# Revit family: xTowel_Dispenser-Automatic-Bobrick-ClassicSeries-3974-150
name_source: partatom
category: Specialty Equipment
revit_build: Autodesk Revit 2014 (Build: 20130308_1515(x64)
units: mm (PartAtom-declared; Revit-internal decimal feet)

## types (1)
- 3974-150
    ADA Compliant = Yes
    Assembly Code = E20
    Default Elevation = 44"
    Description = ClassicSeries® Convertible Automatic Universal Roll Paper Towel Module
    Height = 18 1/4"
    Installation Type = Secured to cabinet.
    Length = 9 1/16"
    Manufacturer = Bobrick Washroom Equipment, Inc.
    Material = Stainless Steel-Bobrick-Type 304-Satin
    Model = 3974-150
    Price = Prices may vary. Please consult Manufacturer Representative for most up-to-date price list.
    Product Documentation Link = http://www.bobrick.com
    Product Page URL = http://www.bobrick.com
    Specification = Convertible automatic universal roll paper towel module shall be type-304 stainless steel with all-welded construction; exposed surfaces shall have satin-fi nish. Door shall be secured to cabinet with a full-length stainless steel piano-hinge and equipped with a  concealed tumbler lock keyed like other Bobrick washroom accessories.  No-touch dispenser, equipped with an intuitive LED light to direct patrons to the dispense area, dispenses universal, 1-1/2" to 2" (38 to 51mm) diameter core, up to 8" (205mm) diameter, 8" (205mm) wide, non-perforated, nonproprietary paper towel rolls, 800 ft (244 m) long. Dispenser automatically dispenses towel when hands are placed under the towel opening. Dispenser can be powered by 4 “D” size alkaline batteries or an optional 6 volt DC power supply. Equipped with switches that allow paper length to be set at 9" (230mm), 12" (305mm) or 15" (380mm) and “Paper Saver” feature that provides a shorter second sheet with options of 25% shorter and 12.5% shorter. LED light at the towel opening fl ashes green when dispenser is ready to dispense, fl ashes orange, indicating low battery, fl ashes red if not ready to dispense or in need of service. Automatic transfer shall dispense stub roll up to 3-1/2" (90mm) diameter before new main roll is automatically dispensed.
    URL = http://www.bobrick.com
    Voltage = 6 V
    Warranty Information = 1 Year Limited Warranty
    Width = 15 3/16"

## geometry (parser evidence)
native form markers: Sweep x2
no freeform markers — native parametric forms only
